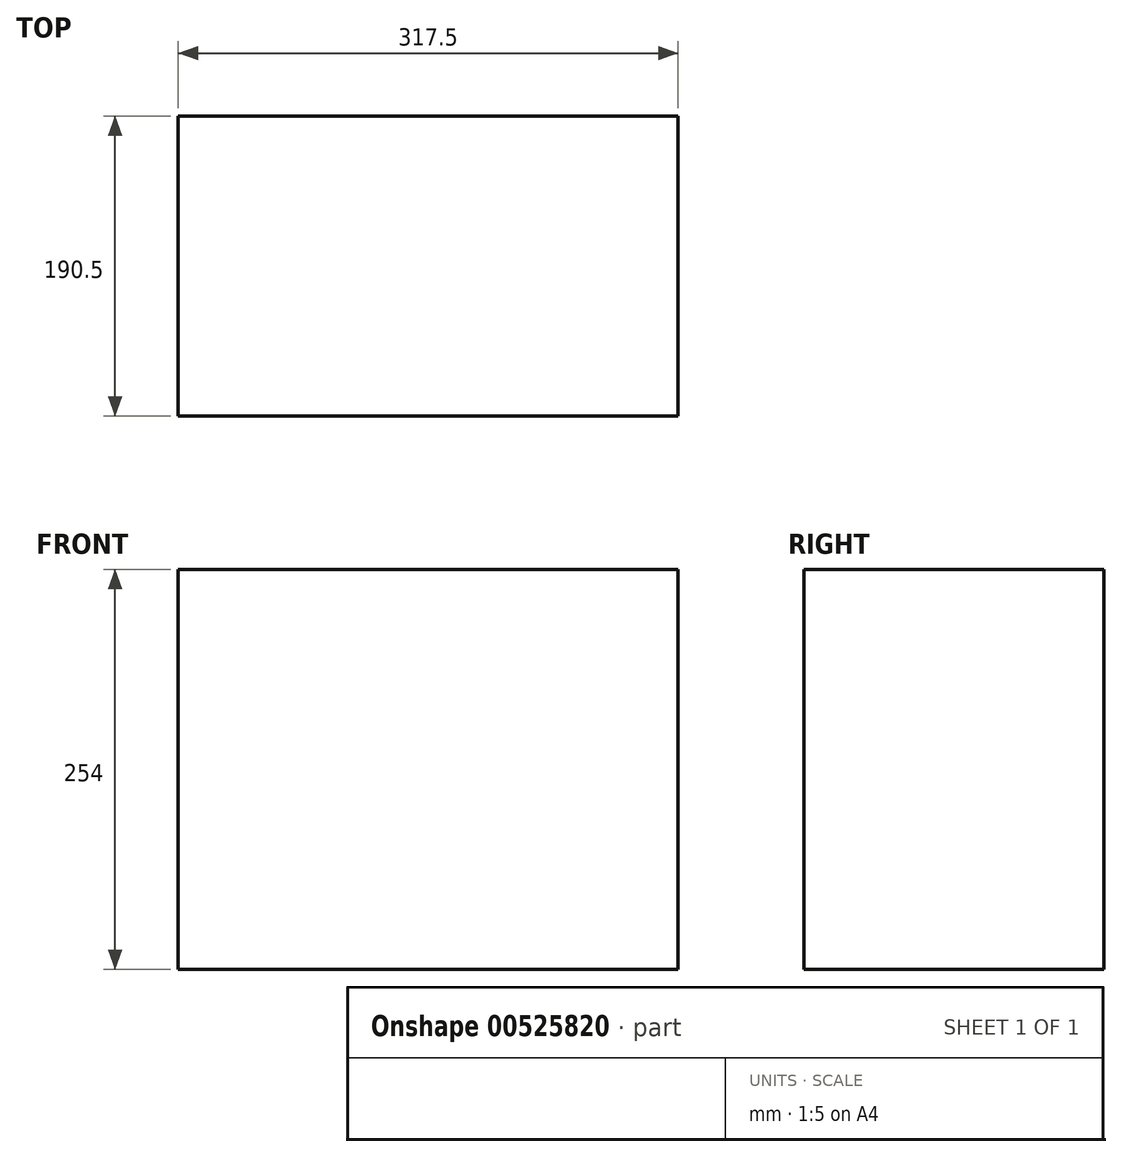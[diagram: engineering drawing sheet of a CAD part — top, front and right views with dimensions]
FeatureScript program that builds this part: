
annotation { "Feature Type Name" : "Feature", "Feature Type Description" : "" }
export const myFeature = defineFeature(function(context is Context, id is Id, definition is map)
    precondition{}
    {
        {
            var Q0;
            Q0=qCreatedBy(makeId("Top.planeOp"),FACE);
            var sketch = newSketch(context, id + "F0", { "sketchPlane" : qUnion([Q0])});
            skLineSegment(sketch, "E0.bottom", {"start": v(158.75, 95.25) * mm, "end": v(-158.75, 95.25) * mm});
            skLineSegment(sketch, "E0.top", {"start": v(158.75, -95.25) * mm, "end": v(-158.75, -95.25) * mm});
            skLineSegment(sketch, "E0.left", {"start": v(158.75, 95.25) * mm, "end": v(158.75, -95.25) * mm});
            skLineSegment(sketch, "E0.right", {"start": v(-158.75, 95.25) * mm, "end": v(-158.75, -95.25) * mm});
            skPoint(sketch, "E0.middle", {"position": v(0, 0) * mm});
            skSolve(sketch);
        }
        {
            var Q0;
            Q0 = qSketchRegion(id + "F0", true);
            extrude(context, id + "F1", {"entities" : qUnion([Q0]), "depth" : 254 * mm, "offsetDistance" : 25.4 * mm});
        }
    });
